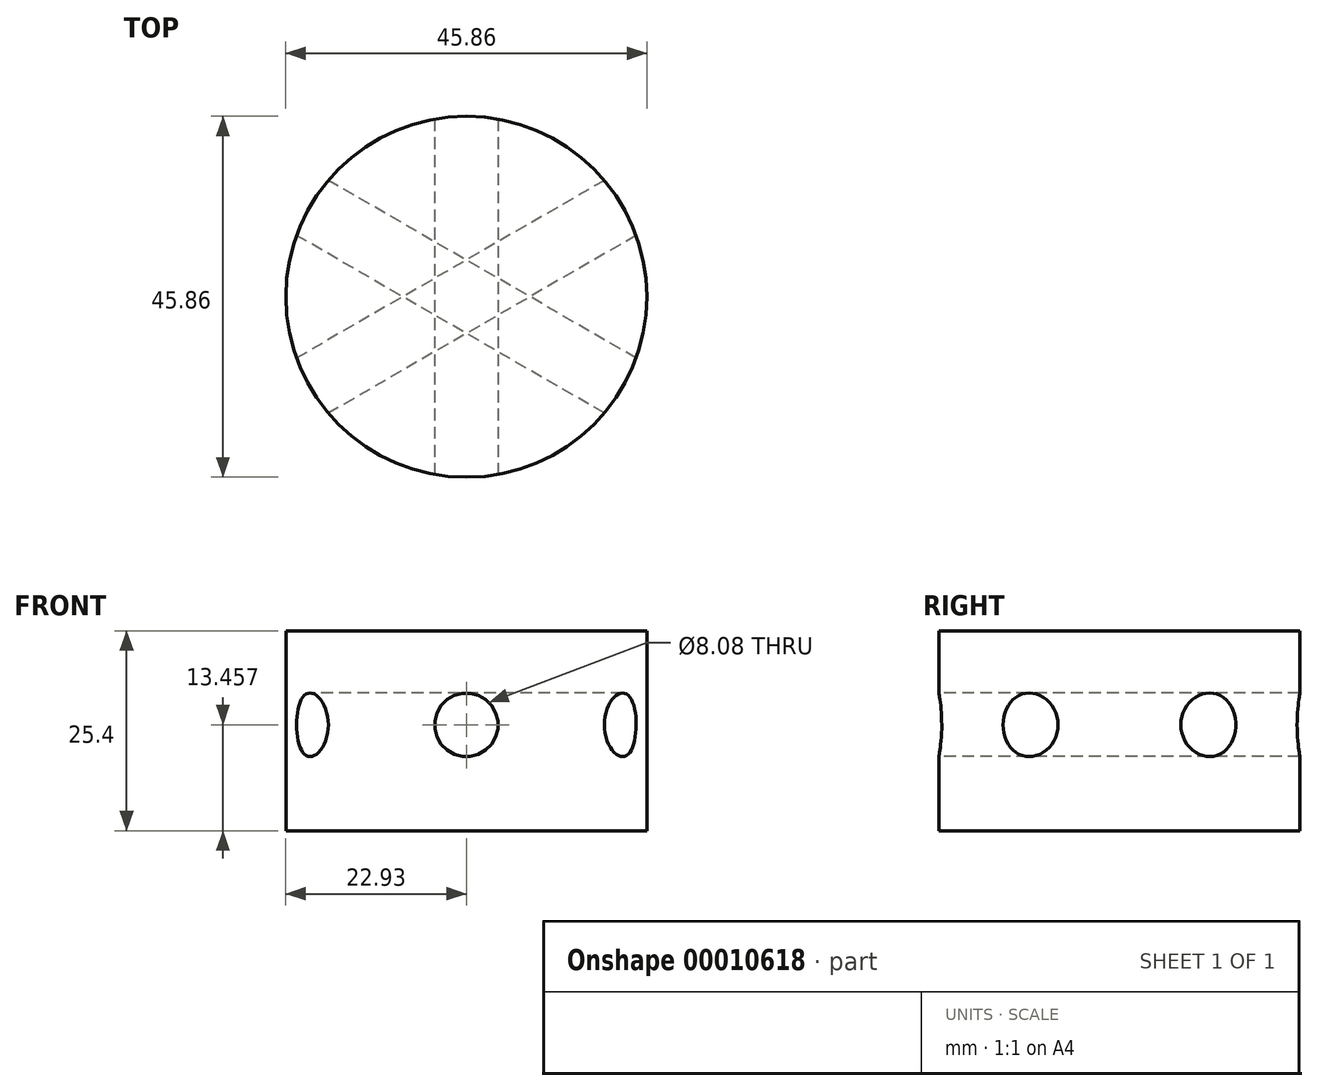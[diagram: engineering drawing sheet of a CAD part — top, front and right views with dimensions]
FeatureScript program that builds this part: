
annotation { "Feature Type Name" : "Feature", "Feature Type Description" : "" }
export const myFeature = defineFeature(function(context is Context, id is Id, definition is map)
    precondition{}
    {
        {
            var Q0;
            Q0=qCreatedBy(makeId("Top.planeOp"),FACE);
            var sketch = newSketch(context, id + "F0", { "sketchPlane" : qUnion([Q0])});
            skCircle(sketch, "E0", {"center": v(0, 0) * mm, "radius": 22.93 * mm});
            skSolve(sketch);
        }
        {
            var Q0;
            Q0=qSketchRegion(id+"F0",true);
            extrude(context, id + "F1", {"entities" : qUnion([Q0]), "depth" : 25.4 * mm});
        }
        {
            var Q0;
            Q0=qCreatedBy(makeId("Front.planeOp"),FACE);
            var sketch = newSketch(context, id + "F2", { "sketchPlane" : qUnion([Q0])});
            skLineSegment(sketch, "E1", {"start": v(0, 0) * mm, "end": v(0, 72.4) * mm, "construction": true});
            skCircle(sketch, "E2", {"center": v(0, 13.46) * mm, "radius": 4.04 * mm});
            skSolve(sketch);
        }
        {
            var Q0;
            Q0=qSketchRegion(id+"F2",true);
            extrude(context, id + "F3", {"entities" : qUnion([Q0]), "operationType" : NewBodyOperationType.REMOVE, "depth" : 50.8 * mm, "symmetric" : true});
        }
        {
            var Q0;
            Q0=makeQuery(id+"F3.boolean.opBoolean","COPY",FACE,{"derivedFrom":makeQuery(id+"F3.opExtrude","SWEPT_FACE",FACE,{"disambiguationData":[OSD([sQuery(id+"F2.wireOp",EDGE,"E2")])]})});
            var Q1;
            Q1=sQuery(id+"F2.wireOp",EDGE,"E1");
            circularPattern(context, id + "F4", {"faces" : qUnion([Q0]), "axis" : qUnion([Q1]), "angle" : 180 * degree, "instanceCount" : round(4), "equalSpace" : true, "patternType" : PatternType.FACE});
        }
    });
